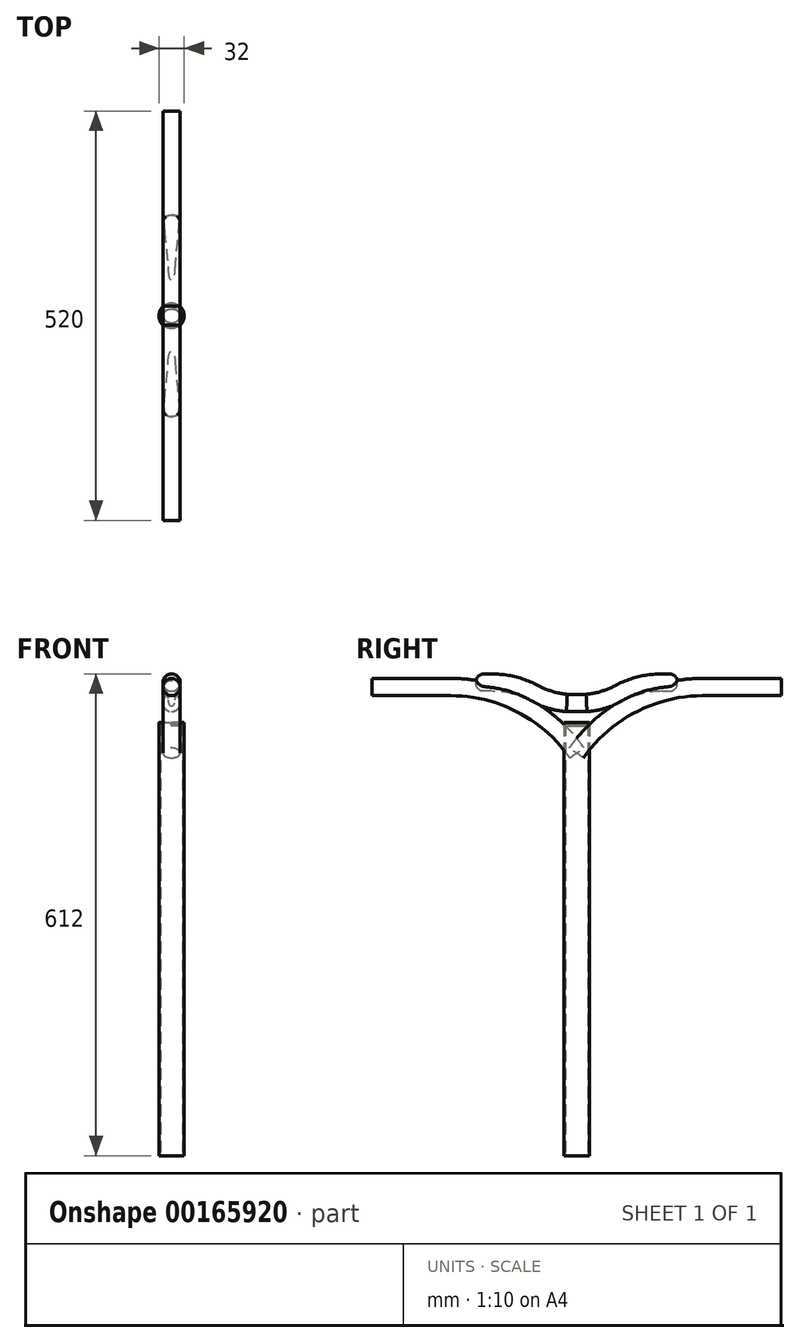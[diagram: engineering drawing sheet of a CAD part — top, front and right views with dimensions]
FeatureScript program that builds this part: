
annotation { "Feature Type Name" : "Feature", "Feature Type Description" : "" }
export const myFeature = defineFeature(function(context is Context, id is Id, definition is map)
    precondition{}
    {
        {
            var Q0;
            Q0=qCreatedBy(makeId("Top.planeOp"),FACE);
            var sketch = newSketch(context, id + "F0", { "sketchPlane" : qUnion([Q0])});
            skCircle(sketch, "E0", {"center": v(0, 0) * mm, "radius": 16 * mm});
            skSolve(sketch);
        }
        {
            var Q0;
            Q0 = qSketchRegion(id + "F0", true);
            extrude(context, id + "F1", {"entities" : qUnion([Q0]), "depth" : 550 * mm});
        }
        {
            var Q0;
            Q0=qCreatedBy(makeId("Right.planeOp"),FACE);
            var sketch = newSketch(context, id + "F2", { "sketchPlane" : qUnion([Q0])});
            skArc(sketch, "E1", {"start": v(160, 595) * mm, "mid": v(69.75, 572.86) * mm, "end": v(0, 511.47) * mm});
            skLineSegment(sketch, "E2", {"start": v(160, 595) * mm, "end": v(260, 595) * mm});
            skSolve(sketch);
        }
        {
            var Q0;
            Q0=sQuery(id+"F2.wireOp",VERTEX,"E2.end");
            var Q1;
            Q1=qCreatedBy(makeId("Front.planeOp"),FACE);
            cPlane(context, id + "F3", {"entities" : qUnion([Q0, Q1]), "cplaneType" : CPlaneType.PLANE_POINT, "offset" : 25 * mm, "width" : 150 * mm, "height" : 150 * mm});
        }
        {
            var Q0;
            Q0=qCreatedBy(id+"F3.planeOp",FACE);
            var sketch = newSketch(context, id + "F4", { "sketchPlane" : qUnion([Q0])});
            skCircle(sketch, "E3", {"center": v(0, 220.01) * mm, "radius": 11 * mm});
            skCircle(sketch, "E4", {"center": v(0, 595.31) * mm, "radius": 11 * mm});
            skSolve(sketch);
        }
        {
            var Q0;
            Q0=makeQuery(id+"F4.imprint","IMPRINT",FACE,{"disambiguationData":[TD([[makeQuery(id+"F4.imprint","IMPRINT",EDGE,{"derivedFrom":sQuery(id+"F4.wireOp",EDGE,"E4")}),1.0]])]});
            var Q1;
            Q1=sQuery(id+"F2.wireOp",EDGE,"E2");
            var Q2;
            Q2=sQuery(id+"F2.wireOp",EDGE,"E1");
            sweep(context, id + "F5", {"profiles" : qUnion([Q0]), "path" : qUnion([Q1, Q2])});
        }
        {
            var Q0;
            Q0=qCreatedBy(makeId("Right.planeOp"),FACE);
            var sketch = newSketch(context, id + "F6", { "sketchPlane" : qUnion([Q0])});
            skLineSegment(sketch, "E5", {"start": v(-128, 601) * mm, "end": v(-108, 601) * mm});
            skArc(sketch, "E6", {"start": v(-54.42, 587.63) * mm, "mid": v(-80.39, 597.6) * mm, "end": v(-108, 601) * mm});
            skArc(sketch, "E7", {"start": v(-54.42, 587.63) * mm, "mid": v(-34.08, 579.24) * mm, "end": v(-12.5, 575) * mm});
            skLineSegment(sketch, "E8", {"start": v(-12.5, 575) * mm, "end": v(0, 575) * mm});
            skLineSegment(sketch, "E9.MirrorCS", {"start": v(12.5, 575) * mm, "end": v(0, 575) * mm});
            skArc(sketch, "E10.MirrorCS", {"start": v(54.42, 587.63) * mm, "mid": v(34.08, 579.24) * mm, "end": v(12.5, 575) * mm});
            skArc(sketch, "E11.MirrorCS", {"start": v(54.42, 587.63) * mm, "mid": v(80.39, 597.6) * mm, "end": v(108, 601) * mm});
            skLineSegment(sketch, "E12.MirrorCS", {"start": v(128, 601) * mm, "end": v(108, 601) * mm});
            skSolve(sketch);
        }
        {
            var Q0;
            Q0=sQuery(id+"F6.wireOp",VERTEX,"E12.MirrorCS.start");
            var Q1;
            Q1=qCreatedBy(makeId("Front.planeOp"),FACE);
            cPlane(context, id + "F7", {"entities" : qUnion([Q0, Q1]), "cplaneType" : CPlaneType.PLANE_POINT, "offset" : 25 * mm, "width" : 150 * mm, "height" : 150 * mm});
        }
        {
            var Q0;
            Q0=qCreatedBy(id+"F7.planeOp",FACE);
            var sketch = newSketch(context, id + "F8", { "sketchPlane" : qUnion([Q0])});
            skCircle(sketch, "E13", {"center": v(0, 601) * mm, "radius": 11 * mm});
            skSolve(sketch);
        }
        {
            var Q0;
            Q0=makeQuery(id+"F8.imprint","IMPRINT",FACE,{"disambiguationData":[TD([[makeQuery(id+"F8.imprint","IMPRINT",EDGE,{"derivedFrom":sQuery(id+"F8.wireOp",EDGE,"E13")}),1.0]])]});
            var Q1;
            Q1=sQuery(id+"F6.wireOp",EDGE,"E11.MirrorCS");
            var Q2;
            Q2=sQuery(id+"F6.wireOp",EDGE,"E10.MirrorCS");
            var Q3;
            Q3=sQuery(id+"F6.wireOp",EDGE,"E9.MirrorCS");
            var Q4;
            Q4=sQuery(id+"F6.wireOp",EDGE,"E8");
            var Q5;
            Q5=sQuery(id+"F6.wireOp",EDGE,"E7");
            var Q6;
            Q6=sQuery(id+"F6.wireOp",EDGE,"E6");
            var Q7;
            Q7=sQuery(id+"F6.wireOp",EDGE,"E5");
            var Q8;
            Q8=sQuery(id+"F6.wireOp",EDGE,"E12.MirrorCS");
            sweep(context, id + "F9", {"operationType" : NewBodyOperationType.ADD, "profiles" : qUnion([Q0]), "path" : qUnion([Q1, Q2, Q3, Q4, Q5, Q6, Q7, Q8])});
        }
        {
            var Q0;
            Q0=makeQuery(id+"F9.opSweep","CAP_EDGE",EDGE,{"disambiguationData":[OSD([sQuery(id+"F6.wireOp",VERTEX,"E12.MirrorCS.start"),sQuery(id+"F8.wireOp",EDGE,"E13")])],"isStart":true});
            var Q1;
            Q1=makeQuery(id+"F9.opSweep","CAP_EDGE",EDGE,{"disambiguationData":[OSD([sQuery(id+"F6.wireOp",VERTEX,"E5.start"),sQuery(id+"F8.wireOp",EDGE,"E13")])],"isStart":false});
            fillet(context, id + "F10", {"entities" : qUnion([Q0, Q1]), "radius" : 10 * mm, "tangentPropagation" : true, "allowEdgeOverflow" : false});
        }
        {
            var Q0;
            Q0=makeQuery(id+"F5.opSweep","SWEPT_BODY",BODY,{"disambiguationData":[OSD([sQuery(id+"F2.wireOp",EDGE,"E1"),sQuery(id+"F4.wireOp",EDGE,"E4")])]});
            var Q1;
            Q1=qCreatedBy(makeId("Front.planeOp"),FACE);
            mirror(context, id + "F11", {"entities" : qUnion([Q0]), "mirrorPlane" : qUnion([Q1])});
        }
        {
            var Q0;
            Q0=makeQuery(id+"F1.opExtrude","CAP_FACE",FACE,{"disambiguationData":[OSD([sQuery(id+"F0.wireOp",EDGE,"E0")])],"isStart":true});
            shell(context, id + "F12", {"entities" : qUnion([Q0]), "thickness" : 2 * mm});
        }
        {
            var Q0;
            Q0=qCreatedBy(makeId("Right.planeOp"),FACE);
            var sketch = newSketch(context, id + "F13", { "sketchPlane" : qUnion([Q0])});
            skArc(sketch, "E14", {"start": v(-20, 563) * mm, "mid": v(-14.14, 548.86) * mm, "end": v(0, 543) * mm});
            skLineSegment(sketch, "E15", {"start": v(-20, 563) * mm, "end": v(0, 563) * mm});
            skLineSegment(sketch, "E16", {"start": v(0, 543) * mm, "end": v(0, 563) * mm});
            skSolve(sketch);
        }
        {
            var Q0;
            Q0 = qSketchRegion(id + "F13", true);
            var Q1;
            Q1=sQuery(id+"F13.wireOp",EDGE,"E16");
            revolve(context, id + "F14", {"operationType" : NewBodyOperationType.REMOVE, "entities" : qUnion([Q0]), "axis" : qUnion([Q1]), "revolveType" : RevolveType.FULL});
        }
        {
            var Q0;
            Q0=makeQuery(id+"F1.opExtrude","CAP_FACE",FACE,{"disambiguationData":[OSD([sQuery(id+"F0.wireOp",EDGE,"E0")])],"isStart":false});
            cPlane(context, id + "F15", {"entities" : qUnion([Q0]), "cplaneType" : CPlaneType.OFFSET, "offset" : 2 * mm, "oppositeDirection" : true, "width" : 150 * mm, "height" : 150 * mm});
        }
        {
            var Q0;
            Q0=qCreatedBy(id+"F15.planeOp",FACE);
            var sketch = newSketch(context, id + "F16", { "sketchPlane" : qUnion([Q0])});
            skCircle(sketch, "E17", {"center": v(0, 0) * mm, "radius": 14 * mm});
            skSolve(sketch);
        }
        {
            var Q0;
            Q0 = qSketchRegion(id + "F16", true);
            extrude(context, id + "F17", {"entities" : qUnion([Q0]), "oppositeDirection" : true, "depth" : 2 * mm});
        }
    });
